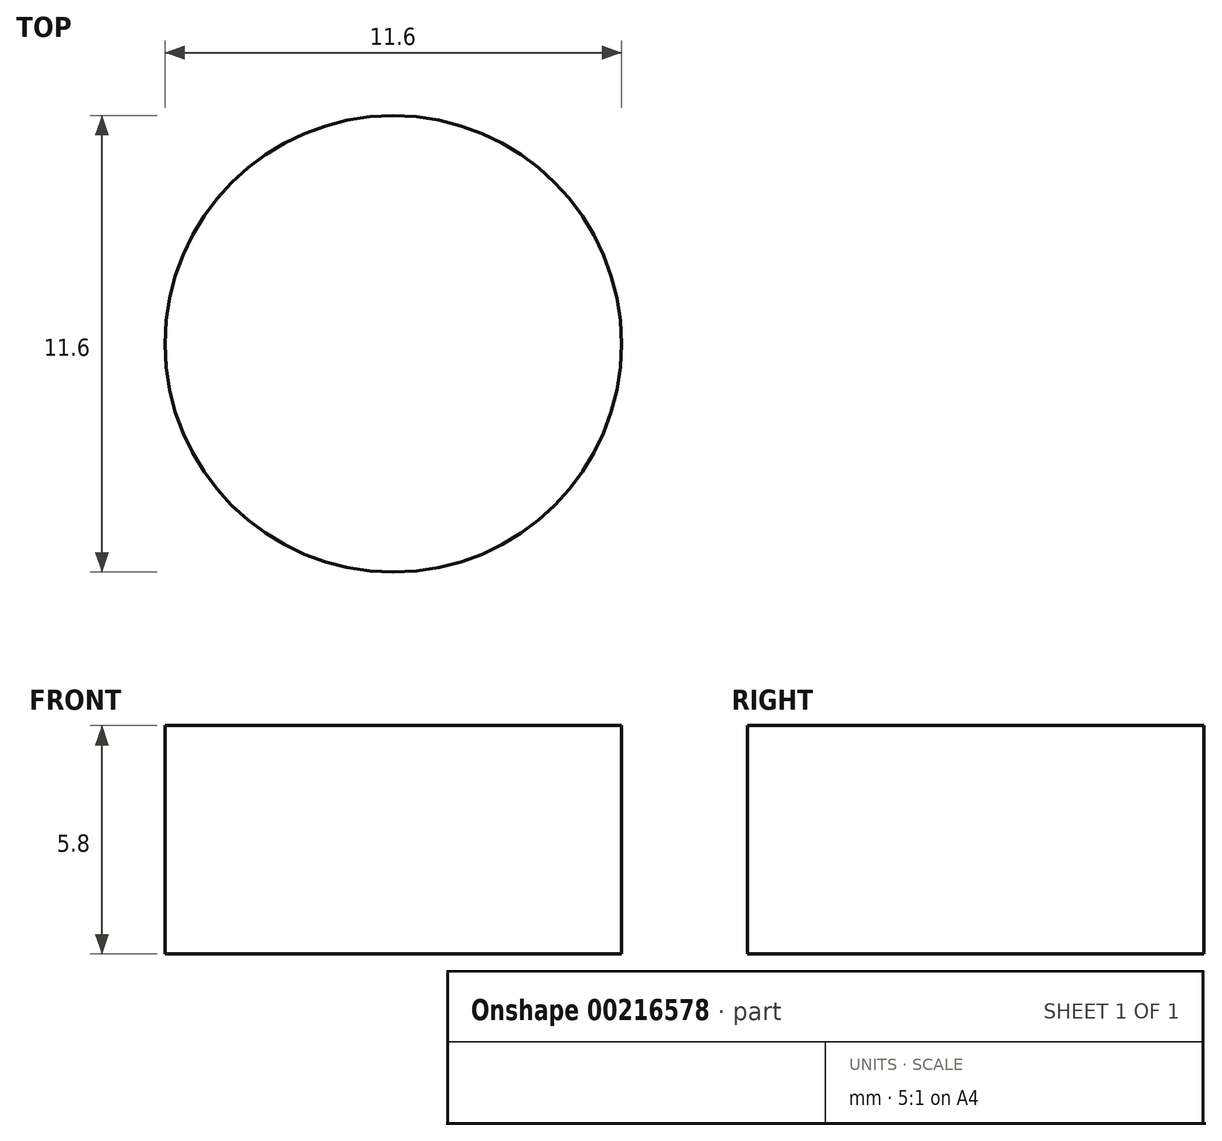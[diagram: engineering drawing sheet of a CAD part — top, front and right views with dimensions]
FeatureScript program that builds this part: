
annotation { "Feature Type Name" : "Feature", "Feature Type Description" : "" }
export const myFeature = defineFeature(function(context is Context, id is Id, definition is map)
    precondition{}
    {
        {
            var Q0;
            Q0=qCreatedBy(makeId("Top.planeOp"),FACE);
            var sketch = newSketch(context, id + "F0", { "sketchPlane" : qUnion([Q0])});
            skCircle(sketch, "E0", {"center": v(0, -1.06) * mm, "radius": 5.8 * mm});
            skSolve(sketch);
        }
        {
            var Q0;
            Q0 = qSketchRegion(id + "F0", true);
            extrude(context, id + "F1", {"entities" : qUnion([Q0]), "depth" : 5.8 * mm});
        }
    });
